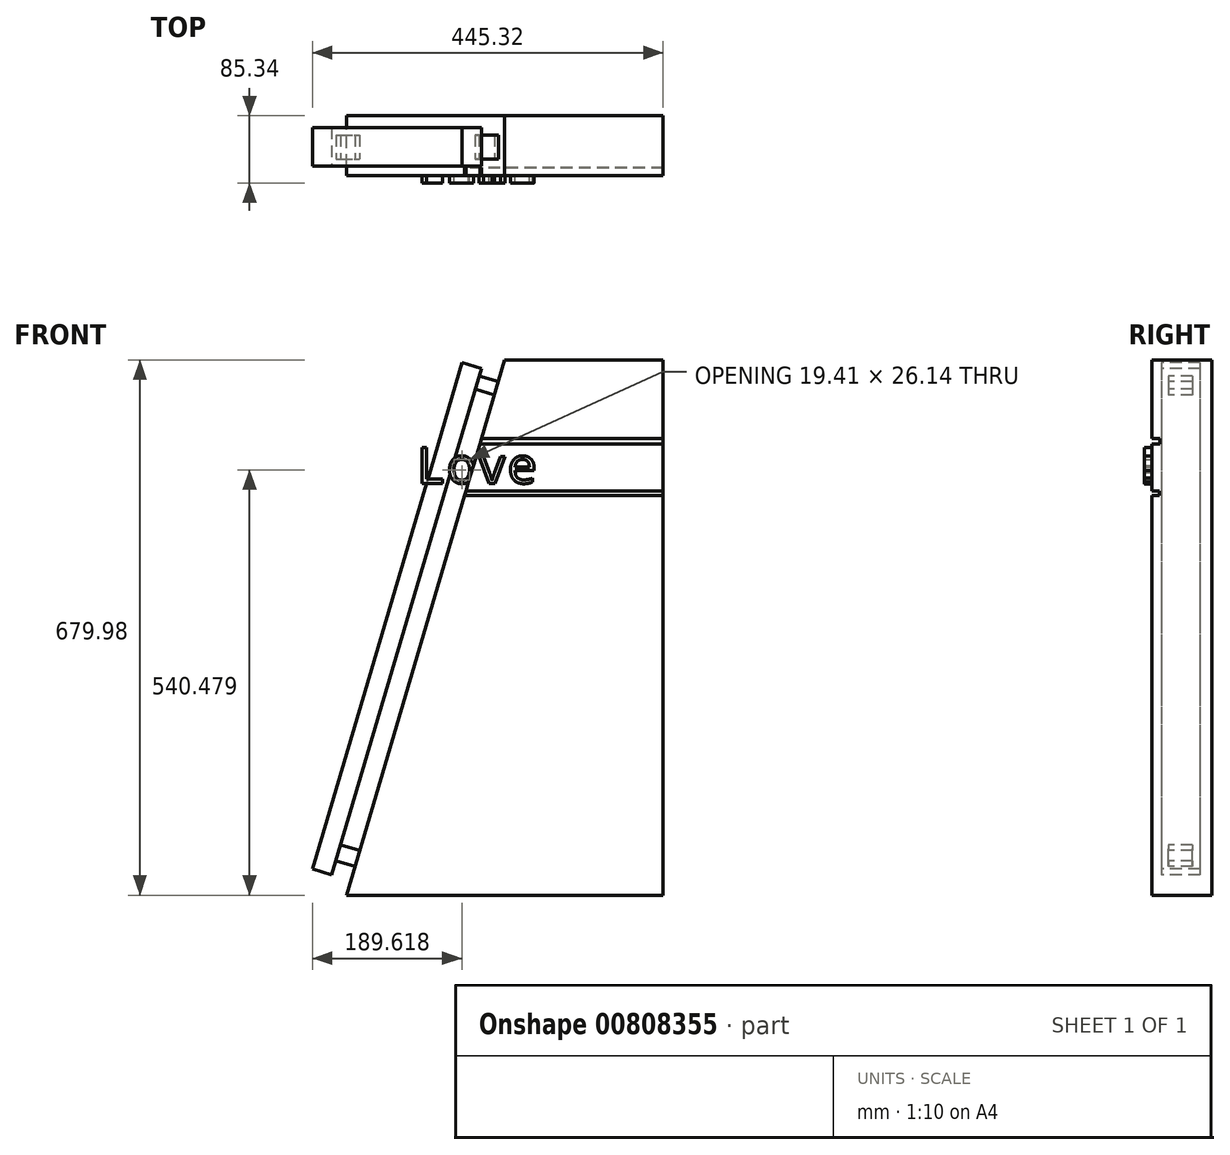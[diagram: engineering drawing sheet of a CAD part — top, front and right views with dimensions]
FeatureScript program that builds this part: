
annotation { "Feature Type Name" : "Feature", "Feature Type Description" : "" }
export const myFeature = defineFeature(function(context is Context, id is Id, definition is map)
    precondition{}
    {
        {
            var Q0;
            Q0=qCreatedBy(makeId("Front.planeOp"),FACE);
            var sketch = newSketch(context, id + "F0", { "sketchPlane" : qUnion([Q0])});
            skLineSegment(sketch, "E0.bottom", {"start": v(-152.93, 156.66) * mm, "end": v(249.27, 156.66) * mm});
            skLineSegment(sketch, "E0.top", {"start": v(-152.93, -523.32) * mm, "end": v(249.27, -523.32) * mm});
            skLineSegment(sketch, "E0.left", {"start": v(-152.93, 156.66) * mm, "end": v(-152.93, -523.32) * mm});
            skLineSegment(sketch, "E0.right", {"start": v(249.27, 156.66) * mm, "end": v(249.27, -523.32) * mm});
            skLineSegment(sketch, "E1", {"start": v(-152.93, -523.32) * mm, "end": v(48.17, 156.66) * mm});
            skSolve(sketch);
        }
        {
            var Q0;
            Q0=makeQuery(id+"F0.imprint","IMPRINT",FACE,{"disambiguationData":[TD([[makeQuery(id+"F0.imprint","IMPRINT",EDGE,{"derivedFrom":sQuery(id+"F0.wireOp",EDGE,"E0.top")}),1.0]])]});
            extrude(context, id + "F1", {"entities" : qUnion([Q0]), "depth" : 76.2 * mm, "offsetDistance" : 25.4 * mm});
        }
        {
            var Q0;
            Q0=makeQuery(id+"F1.opExtrude","CAP_FACE",FACE,{"disambiguationData":[OSD([sQuery(id+"F0.wireOp",EDGE,"E0.bottom"),sQuery(id+"F0.wireOp",EDGE,"E0.top"),sQuery(id+"F0.wireOp",EDGE,"E0.right"),sQuery(id+"F0.wireOp",EDGE,"E1")])],"isStart":false});
            var sketch = newSketch(context, id + "F2", { "sketchPlane" : qUnion([Q0])});
            skLineSegment(sketch, "E2", {"start": v(249.27, 56.97) * mm, "end": v(18.7, 56.97) * mm});
            skLineSegment(sketch, "E3", {"start": v(249.27, 49.93) * mm, "end": v(16.6, 49.93) * mm});
            skLineSegment(sketch, "E4", {"start": v(18.7, 56.97) * mm, "end": v(16.6, 49.93) * mm});
            skLineSegment(sketch, "E5", {"start": v(249.27, 56.97) * mm, "end": v(249.27, 49.93) * mm});
            skSolve(sketch);
        }
        {
            var Q0;
            Q0=makeQuery(id+"F2.imprint","IMPRINT",FACE,{"disambiguationData":[TD([[makeQuery(id+"F2.imprint","IMPRINT",EDGE,{"derivedFrom":sQuery(id+"F2.wireOp",EDGE,"E2")}),1.0]])]});
            extrude(context, id + "F3", {"entities" : qUnion([Q0]), "operationType" : NewBodyOperationType.REMOVE, "oppositeDirection" : true, "depth" : 10.16 * mm, "offsetDistance" : 25.4 * mm});
        }
        {
            var Q0;
            {var subQ0=sQuery(id+"F0.wireOp",EDGE,"E0.top");var subQ1=sQuery(id+"F0.wireOp",EDGE,"E0.right");var subQ2=sQuery(id+"F0.wireOp",EDGE,"E1");Q0=makeQuery(id+"F3.boolean.opBoolean","SPLIT",FACE,{"disambiguationData":[TD([makeQuery(id+"F1.opExtrude","SWEPT_FACE",FACE,{"disambiguationData":[OSD([subQ0])]})])],"derivedFrom":makeQuery(id+"F1.opExtrude","CAP_FACE",FACE,{"disambiguationData":[OSD([sQuery(id+"F0.wireOp",EDGE,"E0.bottom"),subQ0,subQ1,subQ2])],"isStart":false})});}
            var sketch = newSketch(context, id + "F4", { "sketchPlane" : qUnion([Q0])});
            skText(sketch, "E6", { "text": "Love", "fontName": "DroidSansMono.ttf"});
            const initialGuessF4  = {"E6": [-0.06403, 0, 1, 0, 0.04609]};
            skSetInitialGuess(sketch, initialGuessF4);
            skSolve(sketch);
        }
        {
            var Q0;
            Q0=makeQuery(id+"F4.imprint","IMPRINT",FACE,{"disambiguationData":[TD([[makeQuery(id+"F4.imprint","IMPRINT",EDGE,{"derivedFrom":sQuery(id+"F4.wireOp",EDGE,"E6.sketch_text.stroke-28")}),-1.0]])]});
            var Q1;
            Q1=makeQuery(id+"F4.imprint","IMPRINT",FACE,{"disambiguationData":[TD([[makeQuery(id+"F4.imprint","IMPRINT",EDGE,{"derivedFrom":sQuery(id+"F4.wireOp",EDGE,"E6.sketch_text.stroke-18")}),-1.0]])]});
            var Q2;
            Q2=makeQuery(id+"F4.imprint","IMPRINT",FACE,{"disambiguationData":[TD([[makeQuery(id+"F4.imprint","IMPRINT",EDGE,{"derivedFrom":sQuery(id+"F4.wireOp",EDGE,"E6.sketch_text.stroke-6")}),-1.0]])]});
            var Q3;
            Q3=makeQuery(id+"F4.imprint","IMPRINT",FACE,{"disambiguationData":[TD([[makeQuery(id+"F4.imprint","IMPRINT",EDGE,{"derivedFrom":sQuery(id+"F4.wireOp",EDGE,"E6.sketch_text.stroke-0")}),-1.0]])]});
            extrude(context, id + "F5", {"entities" : qUnion([Q0, Q1, Q2, Q3]), "operationType" : NewBodyOperationType.ADD, "depth" : 9.14 * mm, "offsetDistance" : 25.4 * mm});
        }
        {
            var Q0;
            {var subQ0=sQuery(id+"F0.wireOp",EDGE,"E0.right");var subQ2=sQuery(id+"F0.wireOp",EDGE,"E0.top");var subQ3=makeQuery(id+"F1.opExtrude","SWEPT_FACE",FACE,{"disambiguationData":[OSD([subQ2])]});var subQ5=sQuery(id+"F0.wireOp",EDGE,"E1");Q0=makeQuery(id+"F5.boolean.opBoolean","SPLIT",FACE,{"disambiguationData":[TD([subQ3])],"derivedFrom":makeQuery(id+"F3.boolean.opBoolean","SPLIT",FACE,{"disambiguationData":[TD([subQ3])],"derivedFrom":makeQuery(id+"F1.opExtrude","CAP_FACE",FACE,{"disambiguationData":[OSD([sQuery(id+"F0.wireOp",EDGE,"E0.bottom"),subQ2,subQ0,subQ5])],"isStart":false})})});}
            var sketch = newSketch(context, id + "F6", { "sketchPlane" : qUnion([Q0])});
            skLineSegment(sketch, "E7", {"start": v(249.27, -9.6) * mm, "end": v(-1, -9.6) * mm});
            skLineSegment(sketch, "E8", {"start": v(249.27, -15.65) * mm, "end": v(-2.79, -15.65) * mm});
            skLineSegment(sketch, "E9", {"start": v(249.27, -9.6) * mm, "end": v(249.27, -15.65) * mm});
            skLineSegment(sketch, "E10", {"start": v(-1, -9.6) * mm, "end": v(-2.79, -15.65) * mm});
            skSolve(sketch);
        }
        {
            var Q0;
            Q0=makeQuery(id+"F6.imprint","IMPRINT",FACE,{"disambiguationData":[TD([[makeQuery(id+"F6.imprint","IMPRINT",EDGE,{"derivedFrom":sQuery(id+"F6.wireOp",EDGE,"E7")}),1.0]])]});
            extrude(context, id + "F7", {"entities" : qUnion([Q0]), "operationType" : NewBodyOperationType.REMOVE, "oppositeDirection" : true, "depth" : 9.65 * mm, "offsetDistance" : 25.4 * mm});
        }
        {
            var Q0;
            Q0=makeQuery(id+"F1.opExtrude","SWEPT_FACE",FACE,{"disambiguationData":[OSD([sQuery(id+"F0.wireOp",EDGE,"E1")])]});
            var sketch = newSketch(context, id + "F8", { "sketchPlane" : qUnion([Q0])});
            skLineSegment(sketch, "E11.bottom", {"start": v(24.48, 135.3) * mm, "end": v(54.94, 135.3) * mm});
            skLineSegment(sketch, "E11.top", {"start": v(24.48, 117.66) * mm, "end": v(54.94, 117.66) * mm});
            skLineSegment(sketch, "E11.left", {"start": v(24.48, 135.3) * mm, "end": v(24.48, 117.66) * mm});
            skLineSegment(sketch, "E11.right", {"start": v(54.94, 135.3) * mm, "end": v(54.94, 117.66) * mm});
            skPoint(sketch, "E12.oppositeSnap0", {"position": v(54.94, 126.48) * mm});
            skLineSegment(sketch, "E12.bottom", {"start": v(24.48, -506.92) * mm, "end": v(54.94, -506.92) * mm});
            skLineSegment(sketch, "E12.top", {"start": v(24.48, -485.75) * mm, "end": v(54.94, -485.75) * mm});
            skLineSegment(sketch, "E12.left", {"start": v(24.48, -506.92) * mm, "end": v(24.48, -485.75) * mm});
            skLineSegment(sketch, "E12.right", {"start": v(54.94, -506.92) * mm, "end": v(54.94, -485.75) * mm});
            skSolve(sketch);
        }
        {
            var Q0;
            Q0=makeQuery(id+"F8.imprint","IMPRINT",FACE,{"disambiguationData":[TD([[makeQuery(id+"F8.imprint","IMPRINT",EDGE,{"derivedFrom":sQuery(id+"F8.wireOp",EDGE,"E11.bottom")}),-1.0]])]});
            var Q1;
            Q1=makeQuery(id+"F8.imprint","IMPRINT",FACE,{"disambiguationData":[TD([[makeQuery(id+"F8.imprint","IMPRINT",EDGE,{"derivedFrom":sQuery(id+"F8.wireOp",EDGE,"E12.bottom")}),1.0]])]});
            extrude(context, id + "F9", {"entities" : qUnion([Q0, Q1]), "operationType" : NewBodyOperationType.ADD, "depth" : 25.4 * mm, "offsetDistance" : 25.4 * mm});
        }
        {
            var Q0;
            Q0=makeQuery(id+"F9.opExtrude","CAP_FACE",FACE,{"disambiguationData":[OSD([sQuery(id+"F8.wireOp",EDGE,"E11.bottom"),sQuery(id+"F8.wireOp",EDGE,"E11.top"),sQuery(id+"F8.wireOp",EDGE,"E11.left"),sQuery(id+"F8.wireOp",EDGE,"E11.right")])],"isStart":false});
            var sketch = newSketch(context, id + "F10", { "sketchPlane" : qUnion([Q0])});
            skLineSegment(sketch, "E13.bottom", {"start": v(14.9, 145.27) * mm, "end": v(63.93, 145.27) * mm});
            skLineSegment(sketch, "E13.top", {"start": v(14.9, -525.48) * mm, "end": v(63.93, -525.48) * mm});
            skLineSegment(sketch, "E13.left", {"start": v(14.9, 145.27) * mm, "end": v(14.9, -525.48) * mm});
            skLineSegment(sketch, "E13.right", {"start": v(63.93, 145.27) * mm, "end": v(63.93, -525.48) * mm});
            skSolve(sketch);
        }
        {
            var Q0;
            Q0 = qSketchRegion(id + "F10", true);
            extrude(context, id + "F11", {"entities" : qUnion([Q0]), "operationType" : NewBodyOperationType.ADD, "depth" : 25.4 * mm, "offsetDistance" : 25.4 * mm});
        }
    });
